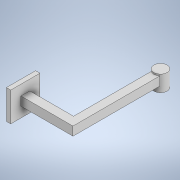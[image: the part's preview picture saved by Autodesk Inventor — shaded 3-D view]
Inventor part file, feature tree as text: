
AUTODESK INVENTOR PART (.ipt)
format: ipt  version: 2020.2 (Build 242310000, 310)  size: 173,568 bytes
history: native  units: in
note: dims shown in document units (in); Inventor stores cm internally (conversion verified against a paired STEP export)
features: extrude x6, sketch x6, projected_geometry x2
ambient origin geometry x8: Origin, YZ Plane, XZ Plane, XY Plane, X Axis, Y Axis, Z Axis, Center Point
bodies: Body1 (feature_tree)
feature tree (14):
  extrude  "Extrusion2"  Depth=0.2047in
  extrude  "Extrusion3"  Depth=0.0394in
  extrude  "Extrusion4"  Depth=0.0394in TaperAngle=0.0deg
  extrude  "Extrusion7"  Depth=0.1181in
  extrude  "Extrusion8"  Depth=0.1181in
  extrude  "Extrusion10"  Depth=0.2362in
  sketch  "Sketch3"  dims[d10=0.3543in d11=0.2047in]
  sketch  "Sketch4"  dims[d12=0.1575in d13=0.0in d14=0.0394in]
  projected_geometry  "Projected Loop1"
  sketch  "Sketch5"  dims[d16=0.2362in d17=0.0in d18=0.0394in d19=0.0in]
  sketch  "Sketch6"  dims[d20=0.0394in d21=0.1181in]
  sketch  "Sketch8"  dims[d22=90.0deg d32=0.1181in]
  projected_geometry  "Projected Loop2"
  sketch  "Sketch10"  dims[d33=180.0deg d34=0.2362in d35=90.0deg d36=0.2362in d37=90.0deg d38=2.4094in d39=0.0in d40=0.2362in d41=1.4in d42=0.0in d49=0.2756in d50=0.2756in d51=90.0deg d52=0.7874in d53=90.0deg d54=0.787in d55=90.0deg d56=90.0deg d57=0.1181in d58=0.0in]
